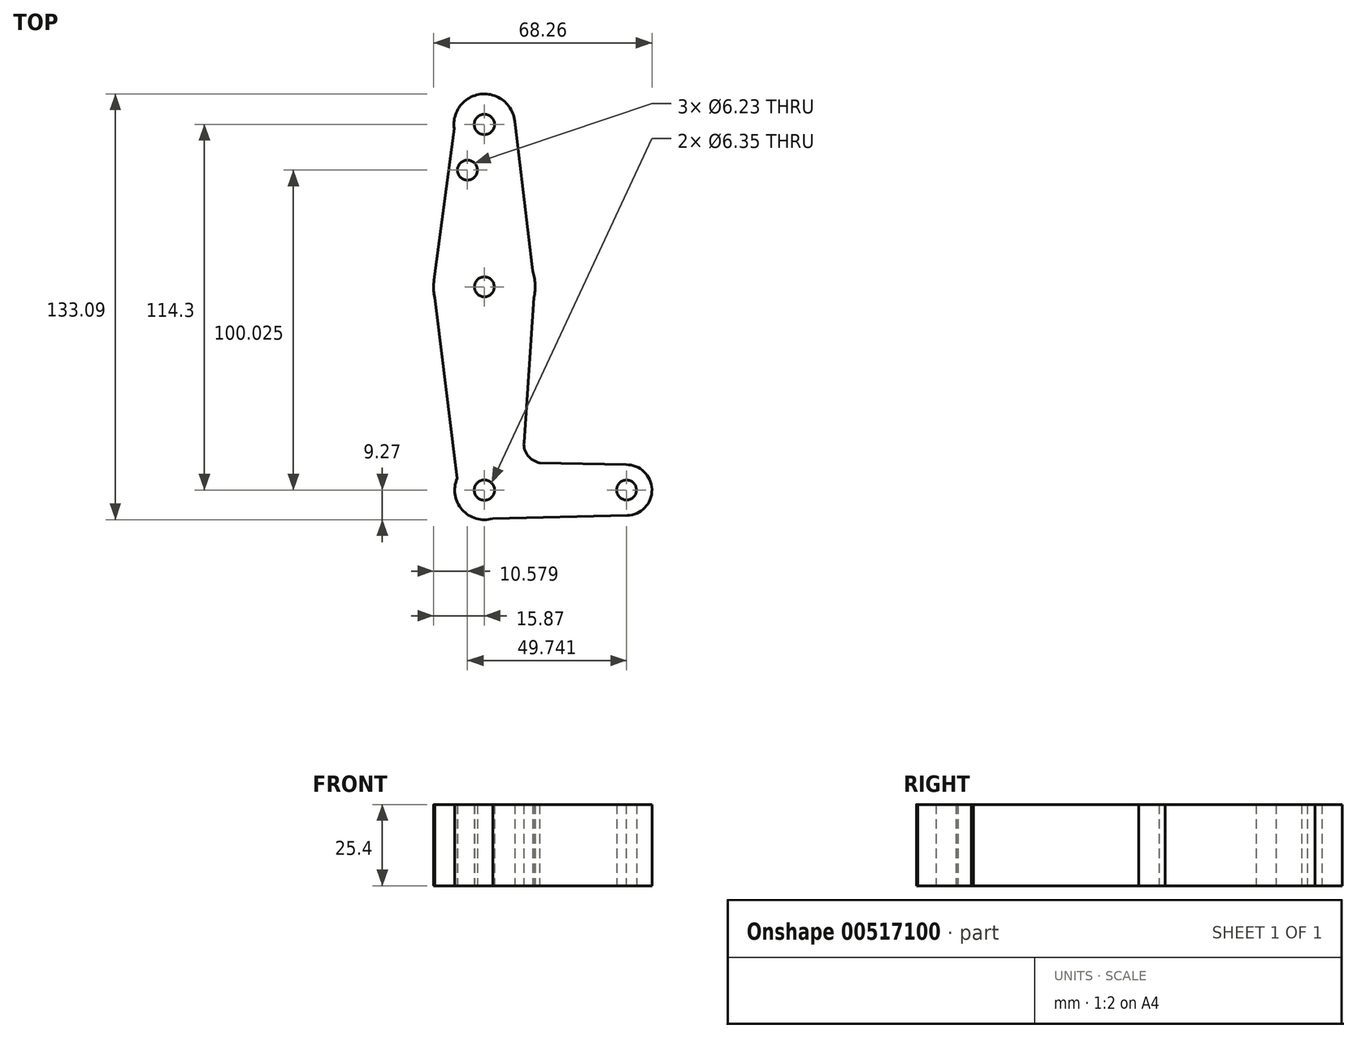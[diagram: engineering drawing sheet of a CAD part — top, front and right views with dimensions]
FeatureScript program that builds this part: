
annotation { "Feature Type Name" : "Feature", "Feature Type Description" : "" }
export const myFeature = defineFeature(function(context is Context, id is Id, definition is map)
    precondition{}
    {
        {
            var Q0;
            Q0=qCreatedBy(makeId("Top.planeOp"),FACE);
            var sketch = newSketch(context, id + "F0", { "sketchPlane" : qUnion([Q0])});
            skCircle(sketch, "E0", {"center": v(0, 0) * mm, "radius": 15.88 * mm});
            skCircle(sketch, "E1", {"center": v(0, 50.8) * mm, "radius": 9.53 * mm});
            skCircle(sketch, "E2", {"center": v(0, 50.8) * mm, "radius": 3.18 * mm});
            skCircle(sketch, "E3", {"center": v(0, 0) * mm, "radius": 3.11 * mm});
            skCircle(sketch, "E4", {"center": v(0, -63.5) * mm, "radius": 9.27 * mm});
            skCircle(sketch, "E5", {"center": v(0, -63.5) * mm, "radius": 3.18 * mm});
            skCircle(sketch, "E6", {"center": v(44.45, -63.5) * mm, "radius": 7.94 * mm});
            skCircle(sketch, "E7", {"center": v(44.45, -63.5) * mm, "radius": 3.11 * mm});
            skCircle(sketch, "E8", {"center": v(-5.3, 36.53) * mm, "radius": 3.11 * mm});
            skLineSegment(sketch, "E9", {"start": v(-9.43, 49.47) * mm, "end": v(-16.01, 0) * mm});
            skLineSegment(sketch, "E10", {"start": v(-15.52, -3.32) * mm, "end": v(-8.5, -59.8) * mm});
            skLineSegment(sketch, "E11", {"start": v(9.47, 51.8) * mm, "end": v(15.06, 5.01) * mm});
            skLineSegment(sketch, "E12", {"start": v(2.6, -72.4) * mm, "end": v(44.63, -71.44) * mm});
            skLineSegment(sketch, "E13", {"start": v(15.52, -3.32) * mm, "end": v(12.38, -48.64) * mm});
            skArc(sketch, "E14", {"start": v(12.38, -48.64) * mm, "mid": v(13.62, -52.74) * mm, "end": v(17.27, -54.97) * mm});
            skLineSegment(sketch, "E15", {"start": v(17.27, -54.97) * mm, "end": v(44.96, -55.58) * mm});
            skSolve(sketch);
        }
        {
            var Q0;
            Q0 = qSketchRegion(id + "F0", true);
            extrude(context, id + "F1", {"entities" : qUnion([Q0]), "depth" : 25.4 * mm, "offsetDistance" : 25.4 * mm});
        }
    });
